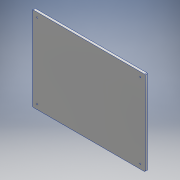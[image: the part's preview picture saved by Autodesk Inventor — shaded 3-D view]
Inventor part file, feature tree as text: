
AUTODESK INVENTOR PART (.ipt)
format: ipt  version: 2016 (Build 200138000, 138)  size: 113,664 bytes
history: native  units: mm
features: sketch x2, extrude x1, fillet x1, hole x1
ambient origin geometry x8: Origin, YZ Plane, XZ Plane, XY Plane, X Axis, Y Axis, Z Axis, Center Point
bodies: Solid1 (feature_tree)
feature tree (5):
  extrude  "Extrusion1"  Depth=450.0mm
  fillet  "Fillet1"  Radius=12.7mm
  hole  "Hole1"  [1 undecoded]
  sketch  "Sketch1"  dims[d0=600.0mm d1=450.0mm d2=12.7mm d3=0.0mm]
  sketch  "Sketch2"  dims[d4=3.0mm d5=25.0mm d6=25.0mm d7=6.6mm d8=6.0mm d9=11.0mm d10=6.0mm d11=90.0deg d12=8.0mm d13=20.594885mm]
note: 1 required parameter value undecoded (feature->parameter linkage not recoverable at this tier; creation-order binding heuristic only, values carry confidence <= 0.55)
